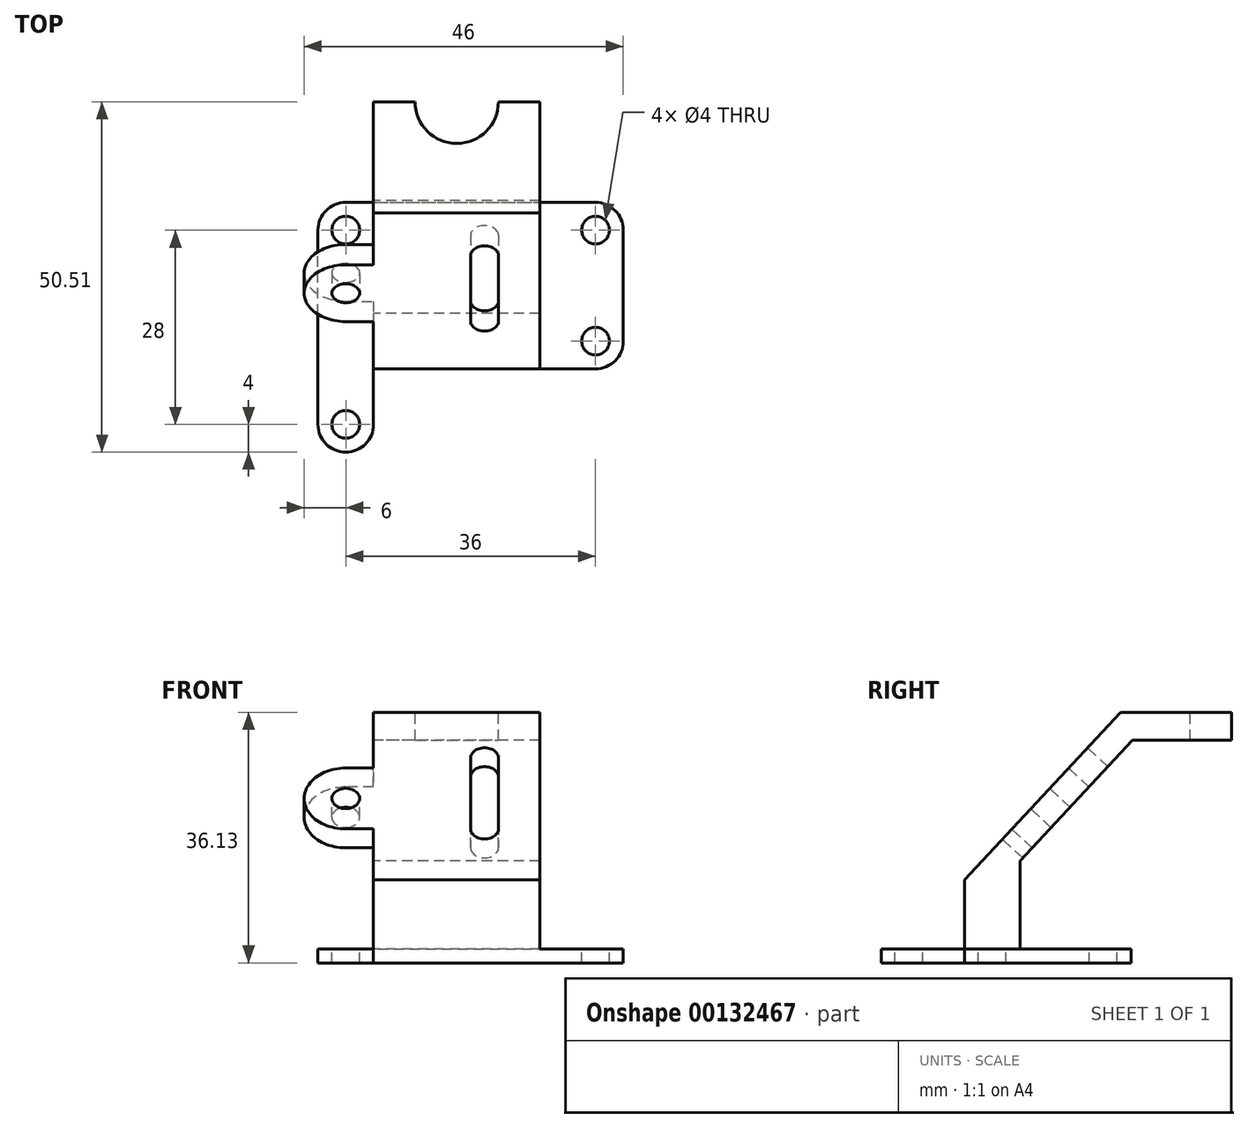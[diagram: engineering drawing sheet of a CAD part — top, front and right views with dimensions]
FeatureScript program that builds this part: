
annotation { "Feature Type Name" : "Feature", "Feature Type Description" : "" }
export const myFeature = defineFeature(function(context is Context, id is Id, definition is map)
    precondition{}
    {
        {
            var Q0;
            Q0=qCreatedBy(makeId("Top.planeOp"),FACE);
            var sketch = newSketch(context, id + "F0", { "sketchPlane" : qUnion([Q0])});
            skLineSegment(sketch, "E0", {"start": v(0, 0) * mm, "end": v(0, 24) * mm});
            skLineSegment(sketch, "E1", {"start": v(0, 24) * mm, "end": v(44, 24) * mm});
            skLineSegment(sketch, "E2", {"start": v(44, 24) * mm, "end": v(44, 0) * mm});
            skLineSegment(sketch, "E3", {"start": v(44, 0) * mm, "end": v(8, 0) * mm});
            skLineSegment(sketch, "E4", {"start": v(8, 0) * mm, "end": v(8, -8) * mm});
            skLineSegment(sketch, "E5", {"start": v(0, 0) * mm, "end": v(0, -8) * mm});
            skArc(sketch, "E6", {"start": v(0, -8) * mm, "mid": v(4, -12) * mm, "end": v(8, -8) * mm});
            skSolve(sketch);
        }
        {
            var Q0;
            Q0 = qSketchRegion(id + "F0", true);
            extrude(context, id + "F1", {"entities" : qUnion([Q0]), "depth" : 2 * mm});
        }
        {
            var Q0;
            Q0=makeQuery(id+"F1.opExtrude","SWEPT_FACE",FACE,{"disambiguationData":[OSD([sQuery(id+"F0.wireOp",EDGE,"E4")])]});
            var sketch = newSketch(context, id + "F2", { "sketchPlane" : qUnion([Q0])});
            skLineSegment(sketch, "E7", {"start": v(0, 2) * mm, "end": v(0, 12) * mm});
            skLineSegment(sketch, "E8", {"start": v(0, 12) * mm, "end": v(22.5, 36.13) * mm});
            skLineSegment(sketch, "E9", {"start": v(22.5, 36.13) * mm, "end": v(38.5, 36.13) * mm});
            skLineSegment(sketch, "E10", {"start": v(38.5, 36.13) * mm, "end": v(38.5, 32.13) * mm});
            skLineSegment(sketch, "E11", {"start": v(38.5, 32.13) * mm, "end": v(24.25, 32.13) * mm});
            skLineSegment(sketch, "E12", {"start": v(24.25, 32.13) * mm, "end": v(8, 14.71) * mm});
            skLineSegment(sketch, "E13", {"start": v(8, 14.71) * mm, "end": v(8, 2) * mm});
            skLineSegment(sketch, "E14", {"start": v(8, 14.71) * mm, "end": v(20.43, 14.71) * mm, "construction": true});
            skLineSegment(sketch, "E15", {"start": v(8, 2) * mm, "end": v(0, 2) * mm});
            skSolve(sketch);
        }
        {
            var Q0;
            Q0 = qSketchRegion(id + "F2", true);
            extrude(context, id + "F3", {"entities" : qUnion([Q0]), "operationType" : NewBodyOperationType.ADD, "depth" : 24 * mm});
        }
        {
            var Q0;
            Q0=makeQuery(id+"F1.opExtrude","CAP_FACE",FACE,{"disambiguationData":[OSD([sQuery(id+"F0.wireOp",EDGE,"E0"),sQuery(id+"F0.wireOp",EDGE,"E1"),sQuery(id+"F0.wireOp",EDGE,"E2"),sQuery(id+"F0.wireOp",EDGE,"E3"),sQuery(id+"F0.wireOp",EDGE,"E4"),sQuery(id+"F0.wireOp",EDGE,"E5"),sQuery(id+"F0.wireOp",EDGE,"E6")])],"isStart":false});
            var sketch = newSketch(context, id + "F4", { "sketchPlane" : qUnion([Q0])});
            skLineSegment(sketch, "E16", {"start": v(8, -8) * mm, "end": v(4, -8) * mm, "construction": true});
            skLineSegment(sketch, "E17", {"start": v(4, -8) * mm, "end": v(0, -8) * mm, "construction": true});
            skCircle(sketch, "E18", {"center": v(4, -8) * mm, "radius": 2 * mm});
            skCircle(sketch, "E19", {"center": v(40, 4) * mm, "radius": 2 * mm});
            skCircle(sketch, "E20", {"center": v(40, 20) * mm, "radius": 2 * mm});
            skCircle(sketch, "E21", {"center": v(4, 20) * mm, "radius": 2 * mm});
            skSolve(sketch);
        }
        {
            var Q0;
            Q0 = qSketchRegion(id + "F4", true);
            extrude(context, id + "F5", {"entities" : qUnion([Q0]), "operationType" : NewBodyOperationType.REMOVE, "endBound" : BoundingType.THROUGH_ALL, "oppositeDirection" : true, "depth" : 25 * mm});
        }
        {
            var Q0;
            Q0=makeQuery(id+"F1.opExtrude","SWEPT_EDGE",EDGE,{"disambiguationData":[OSD([sQuery(id+"F0.wireOp",EDGE,"E2"),sQuery(id+"F0.wireOp",EDGE,"E3")])]});
            var Q1;
            Q1=makeQuery(id+"F1.opExtrude","SWEPT_EDGE",EDGE,{"disambiguationData":[OSD([sQuery(id+"F0.wireOp",EDGE,"E1"),sQuery(id+"F0.wireOp",EDGE,"E2")])]});
            var Q2;
            Q2=makeQuery(id+"F1.opExtrude","SWEPT_EDGE",EDGE,{"disambiguationData":[OSD([sQuery(id+"F0.wireOp",EDGE,"E0"),sQuery(id+"F0.wireOp",EDGE,"E1")])]});
            fillet(context, id + "F6", {"entities" : qUnion([Q0, Q1, Q2]), "radius" : 4 * mm, "tangentPropagation" : true, "allowEdgeOverflow" : false});
        }
        {
            var Q0;
            Q0=makeQuery(id+"F3.opExtrude","SWEPT_FACE",FACE,{"disambiguationData":[OSD([sQuery(id+"F2.wireOp",EDGE,"E9")])]});
            var sketch = newSketch(context, id + "F7", { "sketchPlane" : qUnion([Q0])});
            skArc(sketch, "E22", {"start": v(14, 38.5) * mm, "mid": v(20, 32.5) * mm, "end": v(26, 38.5) * mm});
            skLineSegment(sketch, "E23", {"start": v(26, 38.5) * mm, "end": v(14, 38.5) * mm});
            skSolve(sketch);
        }
        {
            var Q0;
            Q0 = qSketchRegion(id + "F7", true);
            extrude(context, id + "F8", {"entities" : qUnion([Q0]), "operationType" : NewBodyOperationType.REMOVE, "oppositeDirection" : true, "depth" : 4 * mm});
        }
        {
            var Q0;
            Q0=makeQuery(id+"F3.opExtrude","SWEPT_FACE",FACE,{"disambiguationData":[OSD([sQuery(id+"F2.wireOp",EDGE,"E8")])]});
            var sketch = newSketch(context, id + "F9", { "sketchPlane" : qUnion([Q0])});
            skLineSegment(sketch, "E24", {"start": v(8, 30.78) * mm, "end": v(4, 30.78) * mm});
            skLineSegment(sketch, "E25", {"start": v(4, 18.78) * mm, "end": v(8, 18.78) * mm});
            skLineSegment(sketch, "E26", {"start": v(8, 18.78) * mm, "end": v(8, 30.78) * mm});
            skArc(sketch, "E27", {"start": v(4, 30.78) * mm, "mid": v(-2, 24.78) * mm, "end": v(4, 18.78) * mm});
            skCircle(sketch, "E28", {"center": v(4, 24.78) * mm, "radius": 2 * mm});
            skSolve(sketch);
        }
        {
            var Q0;
            Q0 = qSketchRegion(id + "F9", true);
            extrude(context, id + "F10", {"entities" : qUnion([Q0]), "operationType" : NewBodyOperationType.ADD, "oppositeDirection" : true, "depth" : 4 * mm});
        }
        {
            var Q0;
            Q0=makeQuery(id+"F10.boolean.opBoolean","MERGE",FACE,{"derivedFrom":[makeQuery(id+"F3.opExtrude","SWEPT_FACE",FACE,{"disambiguationData":[OSD([sQuery(id+"F2.wireOp",EDGE,"E8")])]}),makeQuery(id+"F10.opExtrude","CAP_FACE",FACE,{"disambiguationData":[OSD([sQuery(id+"F9.wireOp",EDGE,"E24"),sQuery(id+"F9.wireOp",EDGE,"E25"),sQuery(id+"F9.wireOp",EDGE,"E26"),sQuery(id+"F9.wireOp",EDGE,"E27"),sQuery(id+"F9.wireOp",EDGE,"E28")])],"isStart":true})]});
            var sketch = newSketch(context, id + "F11", { "sketchPlane" : qUnion([Q0])});
            skLineSegment(sketch, "E29", {"start": v(26, 32.78) * mm, "end": v(22, 32.78) * mm, "construction": true});
            skArc(sketch, "E30", {"start": v(26, 32.78) * mm, "mid": v(24, 34.78) * mm, "end": v(22, 32.78) * mm});
            skLineSegment(sketch, "E31", {"start": v(26, 32.78) * mm, "end": v(26, 18.78) * mm});
            skLineSegment(sketch, "E32", {"start": v(22, 32.78) * mm, "end": v(22, 18.78) * mm});
            skArc(sketch, "E33", {"start": v(22, 18.78) * mm, "mid": v(24, 16.78) * mm, "end": v(26, 18.78) * mm});
            skSolve(sketch);
        }
        {
            var Q0;
            Q0 = qSketchRegion(id + "F11", true);
            extrude(context, id + "F12", {"entities" : qUnion([Q0]), "operationType" : NewBodyOperationType.REMOVE, "oppositeDirection" : true, "depth" : 4 * mm});
        }
    });
